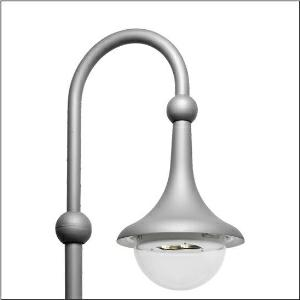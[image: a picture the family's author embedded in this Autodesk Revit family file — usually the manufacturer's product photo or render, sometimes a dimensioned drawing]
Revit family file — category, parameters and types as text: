
# Revit family: grosse_glocke___st1_2a_5xa1563e1b108_a6a2
name_source: partatom
category: Lighting Fixtures
units: mm (PartAtom-declared; Revit-internal decimal feet)

## family parameters
Cut with Voids When Loaded = No
Host = Face
Light Source = No
Part Type = Normal
Room Calculation Point = No
Round Connector Dimension = Use Diameter
Shared = No

## types (1)
- --- (1 x LED, 3150 lm, 23.4 W, 3000K)
    Apparent Load = 23 VA
    CIE Flux Codes = 29 66 95 99 100
    Color Rendering = 70
    Color Temperature = 3000K
    Default Elevation = 1800 mm
    Description = Large Bell, mast luminaire, primary light control with 3 zone facetted reflector, of plastic, silver coated, primary optical cover: enclosure, of PMMA, transparent, light distribution: ST1.2a, light emission: direct distribution, primary light characteristic: asymmetric, installation type: suspended mounting, LED, High Power LED, rated luminous flux: 3.150lm, luminous efficacy: 135lm/W, light colour: 730, colour temperature: 3000K, control gear: ECG Plus, control: flexible luminous flux parameterisation, time-dependent luminous flux control, constant luminous flux control, digital communication interface, power reduction, electronic power reduction, mains connection: 230..240V, AC, 50/60Hz, start of lifetime: 23W, end of service life: 24W, reduction: 12W, luminaire housing, bell-shaped, of glass-fibre reinforced polyester, coated, Siteco® metallic grey (DB 702S), please order curved mast extension separately, diameter: 530mm, height: 695mm, protection rating (complete): IP54, insulation class (complete): insulation class II (safety insulation), certification: CE, ENEC, VDE, impact resistance: IK08, standard-compliant lighting for roads and squares, packaging unit: 1 piece

Light Distribution: ST1.2a
    Height = 695 mm
    Lamp = 1 x LED
    Lamp Light Flux = 3150 lm
    Lamp Power = 23.4 W
    Lamp count = 1
    Length = 530 mm
    Luminous efficacy = 135 lm/W
    Manufacturer = Siteco
    ModVariant = No
    Model = 5XA1563E1B108
    Number of Poles = 1
    OnlyDefault = Yes
    Power Factor = 1
    Product Name = Große Glocke | ST1.2a
    Product group = mast luminaire | pylon annexe
    ProductGroupID = 6201
    Protection Class = Protection class II
    Protection Degree = IP 54
    RLX_Detail_Level = 1
    RLX_Emergency_Light_Flux = 0 lm
    RLX_Emergency_Type = 0
    RLX_Emergency_Type_DB = No
    RlxData = <blob elided: 52949 chars, md5=4c3f3191>
    Socket = socket
    Standby Power = 0 W
    System Light Flux = 3150 lm
    System Power = 23 W
    Type Comments = factory setting: luminous flux: 100 % | dim-lin: 254 | 460 mA
    Type Image = l_1284381.jpg
    URL = http://relux.com
    VarID = @adj_109139
    Voltage = 0 V
    Weight = 0.00 kg
    Width = 0 mm  [stored 0 ft]

note: [stored X ft] marks values corroborated as IEEE doubles in the binary element streams (Revit-internal decimal feet)

## geometry (parser evidence)
native form markers: Blend x4, Sweep x11
no freeform markers — native parametric forms only
